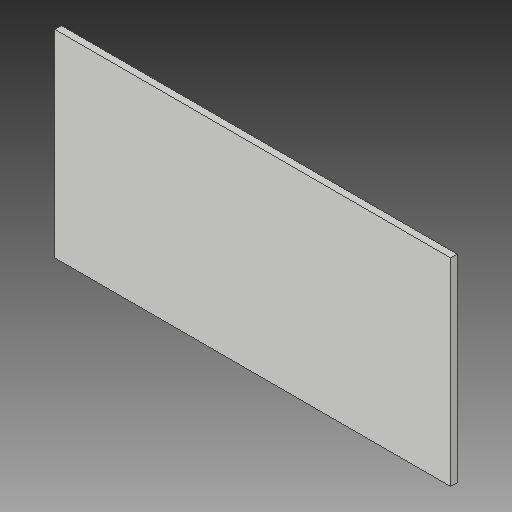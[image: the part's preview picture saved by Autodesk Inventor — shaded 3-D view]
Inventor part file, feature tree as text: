
AUTODESK INVENTOR PART (.ipt)
format: ipt  version: 2017 (Build 210142000, 142)  size: 90,112 bytes
history: native  units: in
note: dims shown in document units (in); Inventor stores cm internally (conversion verified against a paired STEP export)
features: sketch x2, extrude x1, direct_edit x1, hole x1, move_body x1
ambient origin geometry x8: Origin, YZ Plane, XZ Plane, XY Plane, X Axis, Y Axis, Z Axis, Center Point
bodies: Solid1 (feature_tree)
feature tree (6):
  extrude  "Extrusion1"  Depth=3.0in
  sketch  "Sketch2"  dims[d2=0.1in d3=0.0in d4=0.0in d5=0.0in d6=-3.0in d7=0.25in d8=0.75in d9=0.375in d10=0.25in d11=0.5635in d12=1.0in d13=0.8108in]
  direct_edit  "Direct Edit1"
  hole  "Hole1"  [1 undecoded]
  sketch  "Sketch1"  dims[d0=9.0in d1=3.0in]
  move_body  "Move1"
note: 1 required parameter value undecoded (feature->parameter linkage not recoverable at this tier; creation-order binding heuristic only, values carry confidence <= 0.55)
